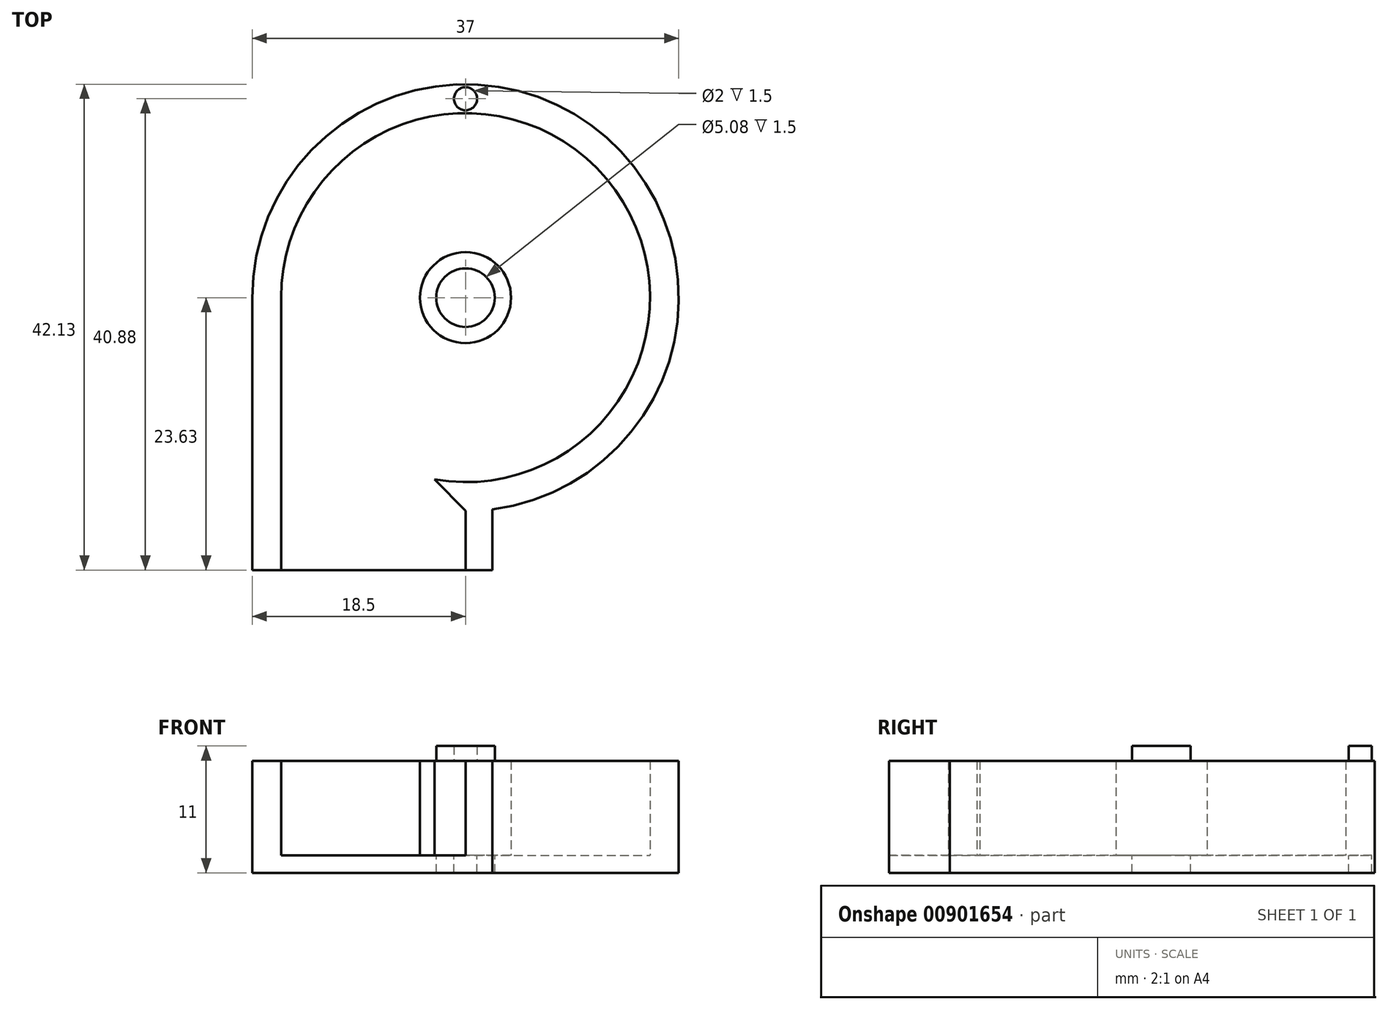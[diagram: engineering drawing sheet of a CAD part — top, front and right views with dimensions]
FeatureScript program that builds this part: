
annotation { "Feature Type Name" : "Feature", "Feature Type Description" : "" }
export const myFeature = defineFeature(function(context is Context, id is Id, definition is map)
    precondition{}
    {
        {
            var Q0;
            Q0=qCreatedBy(makeId("Top.planeOp"),FACE);
            var sketch = newSketch(context, id + "F0", { "sketchPlane" : qUnion([Q0])});
            skCircle(sketch, "E0", {"center": v(0, 0) * mm, "radius": 16 * mm});
            skCircle(sketch, "E1", {"center": v(0, 0) * mm, "radius": 3.95 * mm});
            skCircle(sketch, "E2", {"center": v(0, 0) * mm, "radius": 18.5 * mm});
            skLineSegment(sketch, "E3", {"start": v(-16, 0) * mm, "end": v(-16, -23.63) * mm});
            skLineSegment(sketch, "E4", {"start": v(-16, -23.63) * mm, "end": v(0, -23.63) * mm});
            skLineSegment(sketch, "E5", {"start": v(0, -23.63) * mm, "end": v(0, -20.05) * mm});
            skLineSegment(sketch, "E6", {"start": v(0, -18.5) * mm, "end": v(-2.69, -15.77) * mm});
            skLineSegment(sketch, "E7", {"start": v(0, -20.05) * mm, "end": v(0, -18.5) * mm});
            skLineSegment(sketch, "E8", {"start": v(-18.5, 0) * mm, "end": v(-18.5, -23.63) * mm});
            skLineSegment(sketch, "E9", {"start": v(-18.5, -23.63) * mm, "end": v(-16, -23.63) * mm});
            skLineSegment(sketch, "E10", {"start": v(0, -16) * mm, "end": v(2.32, -18.35) * mm});
            skLineSegment(sketch, "E11", {"start": v(2.32, -18.35) * mm, "end": v(2.32, -23.63) * mm});
            skLineSegment(sketch, "E12", {"start": v(2.32, -23.63) * mm, "end": v(0, -23.63) * mm});
            skLineSegment(sketch, "E13", {"start": v(-16, 0) * mm, "end": v(-18.5, 0) * mm});
            skCircle(sketch, "E14", {"center": v(0, 0) * mm, "radius": 2.54 * mm});
            skCircle(sketch, "E15", {"center": v(0, 17.25) * mm, "radius": 1 * mm});
            skLineSegment(sketch, "E16", {"start": v(0, 18.5) * mm, "end": v(0, 18.25) * mm, "construction": true});
            skLineSegment(sketch, "E17", {"start": v(0, 16.25) * mm, "end": v(0, 16) * mm, "construction": true});
            skSolve(sketch);
        }
        {
            var Q0;
            {var subQ3=sQuery(id+"F0.wireOp",EDGE,"E6");Q0=makeQuery(id+"F0.imprint","IMPRINT",FACE,{"disambiguationData":[TD([[makeQuery(id+"F0.imprint","IMPRINT",EDGE,{"derivedFrom":subQ3}),-1.0]])]});}
            var Q1;
            {var subQ0=sQuery(id+"F0.wireOp",EDGE,"E4");Q1=makeQuery(id+"F0.imprint","IMPRINT",FACE,{"disambiguationData":[TD([[makeQuery(id+"F0.imprint","IMPRINT",EDGE,{"derivedFrom":subQ0}),1.0]])]});}
            var Q2;
            {var subQ3=sQuery(id+"F0.wireOp",EDGE,"E6");Q2=makeQuery(id+"F0.imprint","IMPRINT",FACE,{"disambiguationData":[TD([[makeQuery(id+"F0.imprint","IMPRINT",EDGE,{"derivedFrom":subQ3}),1.0]])]});}
            var Q3;
            Q3=makeQuery(id+"F0.imprint","IMPRINT",FACE,{"disambiguationData":[TD([[makeQuery(id+"F0.imprint","IMPRINT",EDGE,{"derivedFrom":sQuery(id+"F0.wireOp",EDGE,"E1")}),-1.0]])]});
            var Q4;
            Q4=makeQuery(id+"F0.imprint","IMPRINT",FACE,{"disambiguationData":[TD([[makeQuery(id+"F0.imprint","IMPRINT",EDGE,{"derivedFrom":sQuery(id+"F0.wireOp",EDGE,"E1")}),1.0]])]});
            var Q5;
            {var subQ2=sQuery(id+"F0.wireOp",EDGE,"E10");Q5=makeQuery(id+"F0.imprint","IMPRINT",FACE,{"disambiguationData":[TD([[makeQuery(id+"F0.imprint","IMPRINT",EDGE,{"derivedFrom":subQ2}),1.0]])]});}
            var Q6;
            {var subQ0=sQuery(id+"F0.wireOp",EDGE,"E13");Q6=makeQuery(id+"F0.imprint","IMPRINT",FACE,{"disambiguationData":[TD([[makeQuery(id+"F0.imprint","IMPRINT",EDGE,{"derivedFrom":subQ0}),1.0]])]});}
            var Q7;
            {var subQ0=sQuery(id+"F0.wireOp",EDGE,"E8");Q7=makeQuery(id+"F0.imprint","IMPRINT",FACE,{"disambiguationData":[TD([[makeQuery(id+"F0.imprint","IMPRINT",EDGE,{"derivedFrom":subQ0}),1.0]])]});}
            var Q8;
            Q8=makeQuery(id+"F0.imprint","IMPRINT",FACE,{"disambiguationData":[TD([[makeQuery(id+"F0.imprint","IMPRINT",EDGE,{"derivedFrom":sQuery(id+"F0.wireOp",EDGE,"E5")}),-1.0]])]});
            extrude(context, id + "F1", {"entities" : qUnion([Q0, Q1, Q2, Q3, Q4, Q5, Q6, Q7, Q8]), "oppositeDirection" : true, "depth" : 1.5 * mm, "offsetDistance" : 25.4 * mm});
        }
        {
            var Q0;
            {var subQ0=sQuery(id+"F0.wireOp",EDGE,"E8");Q0=makeQuery(id+"F0.imprint","IMPRINT",FACE,{"disambiguationData":[TD([[makeQuery(id+"F0.imprint","IMPRINT",EDGE,{"derivedFrom":subQ0}),1.0]])]});}
            var Q1;
            {var subQ0=sQuery(id+"F0.wireOp",EDGE,"E13");Q1=makeQuery(id+"F0.imprint","IMPRINT",FACE,{"disambiguationData":[TD([[makeQuery(id+"F0.imprint","IMPRINT",EDGE,{"derivedFrom":subQ0}),1.0]])]});}
            var Q2;
            {var subQ2=sQuery(id+"F0.wireOp",EDGE,"E10");Q2=makeQuery(id+"F0.imprint","IMPRINT",FACE,{"disambiguationData":[TD([[makeQuery(id+"F0.imprint","IMPRINT",EDGE,{"derivedFrom":subQ2}),1.0]])]});}
            var Q3;
            Q3=makeQuery(id+"F0.imprint","IMPRINT",FACE,{"disambiguationData":[TD([[makeQuery(id+"F0.imprint","IMPRINT",EDGE,{"derivedFrom":sQuery(id+"F0.wireOp",EDGE,"E5")}),-1.0]])]});
            var Q4;
            {var subQ0=sQuery(id+"F0.wireOp",EDGE,"E6");Q4=makeQuery(id+"F0.imprint","IMPRINT",FACE,{"disambiguationData":[TD([[makeQuery(id+"F0.imprint","IMPRINT",EDGE,{"derivedFrom":subQ0}),-1.0]])]});}
            var Q5;
            Q5=makeQuery(id+"F0.imprint","IMPRINT",FACE,{"disambiguationData":[TD([[makeQuery(id+"F0.imprint","IMPRINT",EDGE,{"derivedFrom":sQuery(id+"F0.wireOp",EDGE,"E1")}),1.0]])]});
            extrude(context, id + "F2", {"entities" : qUnion([Q0, Q1, Q2, Q3, Q4, Q5]), "operationType" : NewBodyOperationType.ADD, "depth" : 8.2 * mm, "offsetDistance" : 25.4 * mm});
        }
        {
            var Q0;
            Q0=makeQuery(id+"F0.imprint","IMPRINT",FACE,{"disambiguationData":[TD([[makeQuery(id+"F0.imprint","IMPRINT",EDGE,{"derivedFrom":sQuery(id+"F0.wireOp",EDGE,"E15")}),1.0]])]});
            var Q1;
            Q1=makeQuery(id+"F0.imprint","IMPRINT",FACE,{"disambiguationData":[TD([[makeQuery(id+"F0.imprint","IMPRINT",EDGE,{"derivedFrom":sQuery(id+"F0.wireOp",EDGE,"E14")}),1.0]])]});
            extrude(context, id + "F3", {"entities" : qUnion([Q0, Q1]), "operationType" : NewBodyOperationType.ADD, "depth" : 9.5 * mm, "offsetDistance" : 25.4 * mm});
        }
    });
